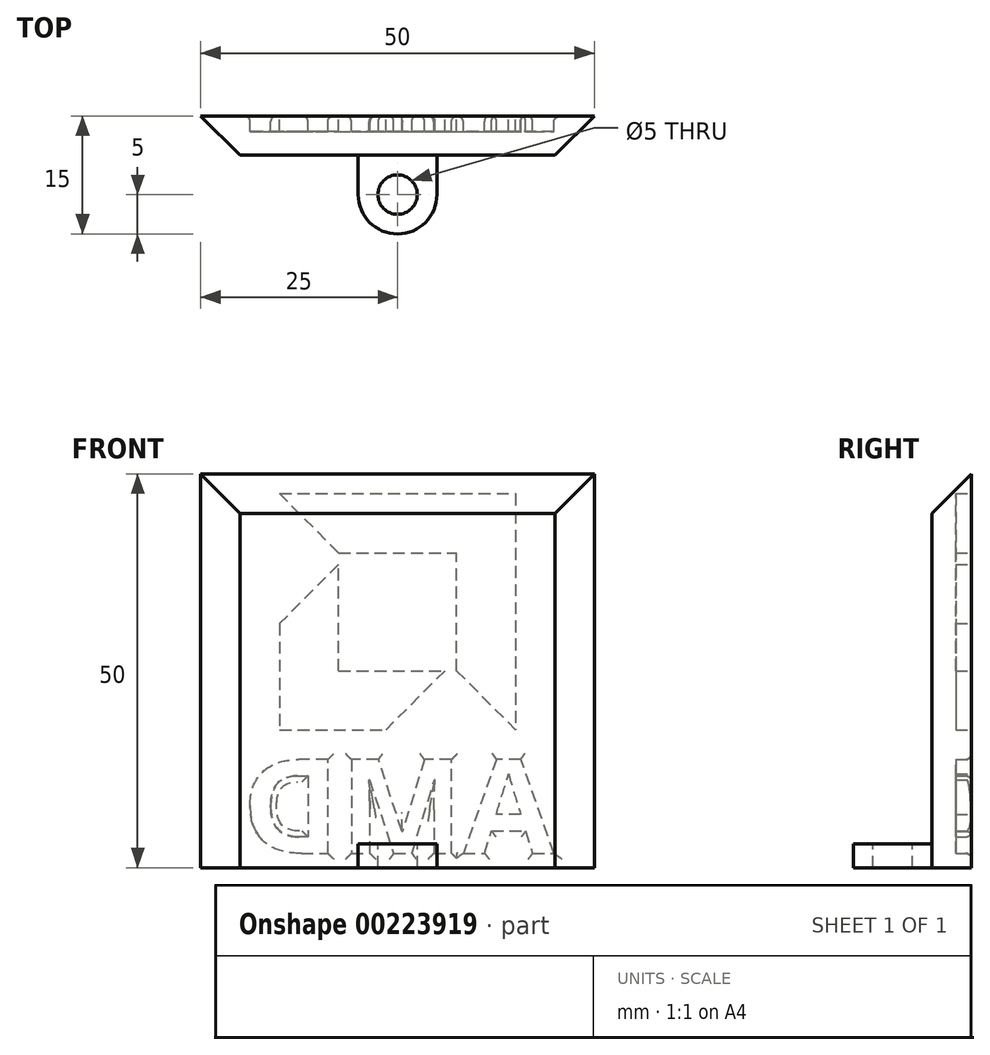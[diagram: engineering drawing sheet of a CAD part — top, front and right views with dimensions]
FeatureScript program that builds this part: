
annotation { "Feature Type Name" : "Feature", "Feature Type Description" : "" }
export const myFeature = defineFeature(function(context is Context, id is Id, definition is map)
    precondition{}
    {
        {
            var Q0;
            Q0=qCreatedBy(makeId("Front.planeOp"),FACE);
            var sketch = newSketch(context, id + "F0", { "sketchPlane" : qUnion([Q0])});
            skLineSegment(sketch, "E0.bottom", {"start": v(0, 0) * mm, "end": v(50, 0) * mm});
            skLineSegment(sketch, "E0.top", {"start": v(0, 50) * mm, "end": v(50, 50) * mm});
            skLineSegment(sketch, "E0.left", {"start": v(0, 0) * mm, "end": v(0, 50) * mm});
            skLineSegment(sketch, "E0.right", {"start": v(50, 0) * mm, "end": v(50, 50) * mm});
            skLineSegment(sketch, "E1.bottom", {"start": v(10, 47.5) * mm, "end": v(40, 47.5) * mm});
            skLineSegment(sketch, "E1.top", {"start": v(10, 17.5) * mm, "end": v(40, 17.5) * mm});
            skLineSegment(sketch, "E1.left", {"start": v(10, 47.5) * mm, "end": v(10, 17.5) * mm});
            skLineSegment(sketch, "E1.right", {"start": v(40, 47.5) * mm, "end": v(40, 17.5) * mm});
            skLineSegment(sketch, "E2.bottom", {"start": v(17.5, 25) * mm, "end": v(32.5, 25) * mm});
            skLineSegment(sketch, "E2.top", {"start": v(17.5, 40) * mm, "end": v(32.5, 40) * mm});
            skLineSegment(sketch, "E2.left", {"start": v(17.5, 25) * mm, "end": v(17.5, 40) * mm});
            skLineSegment(sketch, "E2.right", {"start": v(32.5, 25) * mm, "end": v(32.5, 40) * mm});
            skLineSegment(sketch, "E3", {"start": v(17.5, 40) * mm, "end": v(10, 47.5) * mm});
            skLineSegment(sketch, "E4", {"start": v(32.5, 25) * mm, "end": v(40, 17.5) * mm});
            skPoint(sketch, "E5", {"position": v(17.5, 38.5) * mm});
            skPoint(sketch, "E6", {"position": v(31, 25) * mm});
            skLineSegment(sketch, "E7", {"start": v(17.5, 38.5) * mm, "end": v(10, 31) * mm});
            skLineSegment(sketch, "E8", {"start": v(31, 25) * mm, "end": v(23.5, 17.5) * mm});
            skSolve(sketch);
        }
        {
            var Q0;
            Q0=makeQuery(id+"F0.imprint","IMPRINT",FACE,{"disambiguationData":[TD([[makeQuery(id+"F0.imprint","IMPRINT",EDGE,{"derivedFrom":sQuery(id+"F0.wireOp",EDGE,"E0.bottom")}),1.0]])]});
            var Q1;
            {var subQ0=sQuery(id+"F0.wireOp",EDGE,"E3");Q1=makeQuery(id+"F0.imprint","IMPRINT",FACE,{"disambiguationData":[TD([[makeQuery(id+"F0.imprint","IMPRINT",EDGE,{"derivedFrom":subQ0}),1.0]])]});}
            var Q2;
            Q2=makeQuery(id+"F0.imprint","IMPRINT",FACE,{"disambiguationData":[TD([[makeQuery(id+"F0.imprint","IMPRINT",EDGE,{"derivedFrom":sQuery(id+"F0.wireOp",EDGE,"E1.bottom")}),-1.0]])]});
            var Q3;
            {var subQ4=sQuery(id+"F0.wireOp",EDGE,"E2.top");Q3=makeQuery(id+"F0.imprint","IMPRINT",FACE,{"disambiguationData":[TD([[makeQuery(id+"F0.imprint","IMPRINT",EDGE,{"derivedFrom":subQ4}),-1.0]])]});}
            var Q4;
            {var subQ3=sQuery(id+"F0.wireOp",EDGE,"E7");Q4=makeQuery(id+"F0.imprint","IMPRINT",FACE,{"disambiguationData":[TD([[makeQuery(id+"F0.imprint","IMPRINT",EDGE,{"derivedFrom":subQ3}),1.0]])]});}
            var Q5;
            {var subQ0=sQuery(id+"F0.wireOp",EDGE,"E4");Q5=makeQuery(id+"F0.imprint","IMPRINT",FACE,{"disambiguationData":[TD([[makeQuery(id+"F0.imprint","IMPRINT",EDGE,{"derivedFrom":subQ0}),-1.0]])]});}
            extrude(context, id + "F1", {"entities" : qUnion([Q0, Q1, Q2, Q3, Q4, Q5]), "depth" : 5 * mm});
        }
        {
            var Q0;
            Q0=makeQuery(id+"F0.imprint","IMPRINT",FACE,{"disambiguationData":[TD([[makeQuery(id+"F0.imprint","IMPRINT",EDGE,{"derivedFrom":sQuery(id+"F0.wireOp",EDGE,"E1.bottom")}),-1.0]])]});
            var Q1;
            {var subQ3=sQuery(id+"F0.wireOp",EDGE,"E7");Q1=makeQuery(id+"F0.imprint","IMPRINT",FACE,{"disambiguationData":[TD([[makeQuery(id+"F0.imprint","IMPRINT",EDGE,{"derivedFrom":subQ3}),1.0]])]});}
            extrude(context, id + "F2", {"entities" : qUnion([Q0, Q1]), "operationType" : NewBodyOperationType.REMOVE, "depth" : 2 * mm});
        }
        {
            var Q0;
            Q0=makeQuery(id+"F1.opExtrude","CAP_FACE",FACE,{"disambiguationData":[OSD([sQuery(id+"F0.wireOp",EDGE,"E0.bottom"),sQuery(id+"F0.wireOp",EDGE,"E0.top"),sQuery(id+"F0.wireOp",EDGE,"E0.left"),sQuery(id+"F0.wireOp",EDGE,"E0.right")])],"isStart":true});
            var sketch = newSketch(context, id + "F3", { "sketchPlane" : qUnion([Q0])});
            skText(sketch, "E9", { "text": "AMD", "fontName": "OpenSans-Bold.ttf"});
            const initialGuessF3  = {"E9": [-0.04485, 0.00182, 1, 0, 0.012]};
            skSetInitialGuess(sketch, initialGuessF3);
            skSolve(sketch);
        }
        {
            var Q0;
            Q0 = qSketchRegion(id + "F3", true);
            extrude(context, id + "F4", {"entities" : qUnion([Q0]), "operationType" : NewBodyOperationType.REMOVE, "oppositeDirection" : true, "depth" : 2 * mm});
        }
        {
            var Q0;
            Q0=makeQuery(id+"F1.opExtrude","SWEPT_FACE",FACE,{"disambiguationData":[OSD([sQuery(id+"F0.wireOp",EDGE,"E0.top")])]});
            var sketch = newSketch(context, id + "F5", { "sketchPlane" : qUnion([Q0])});
            skLineSegment(sketch, "E10", {"start": v(0, 0) * mm, "end": v(4.65, -4.65) * mm});
            skLineSegment(sketch, "E11", {"start": v(0, 0) * mm, "end": v(5, -5) * mm});
            skLineSegment(sketch, "E12", {"start": v(5, -5) * mm, "end": v(0, -5) * mm});
            skLineSegment(sketch, "E13", {"start": v(0, -5) * mm, "end": v(0, 0) * mm});
            skLineSegment(sketch, "E14", {"start": v(50, 0) * mm, "end": v(50, -5) * mm});
            skLineSegment(sketch, "E15", {"start": v(50, -5) * mm, "end": v(45, -5) * mm});
            skLineSegment(sketch, "E16", {"start": v(45, -5) * mm, "end": v(50, 0) * mm});
            skSolve(sketch);
        }
        {
            var Q0;
            Q0=makeQuery(id+"F1.opExtrude","SWEPT_FACE",FACE,{"disambiguationData":[OSD([sQuery(id+"F0.wireOp",EDGE,"E0.left")])]});
            var sketch = newSketch(context, id + "F6", { "sketchPlane" : qUnion([Q0])});
            skLineSegment(sketch, "E17", {"start": v(5, 50) * mm, "end": v(5, 45) * mm});
            skLineSegment(sketch, "E18", {"start": v(5, 45) * mm, "end": v(0, 50) * mm});
            skSolve(sketch);
        }
        {
            var Q0;
            Q0 = qSketchRegion(id + "F6", true);
            var Q1;
            Q1=makeQuery(id+"F6.imprint","IMPRINT",FACE,{"disambiguationData":[TD([[makeQuery(id+"F6.imprint","IMPRINT",EDGE,{"derivedFrom":sQuery(id+"F6.wireOp",EDGE,"E17")}),1.0]])]});
            extrude(context, id + "F7", {"entities" : qUnion([Q0, Q1]), "operationType" : NewBodyOperationType.REMOVE, "oppositeDirection" : true, "depth" : 50 * mm});
        }
        {
            var Q0;
            Q0 = qSketchRegion(id + "F5", true);
            extrude(context, id + "F8", {"entities" : qUnion([Q0]), "operationType" : NewBodyOperationType.REMOVE, "oppositeDirection" : true, "depth" : 50 * mm});
        }
        {
            var Q0;
            Q0=makeQuery(id+"F1.opExtrude","CAP_FACE",FACE,{"disambiguationData":[OSD([sQuery(id+"F0.wireOp",EDGE,"E0.bottom"),sQuery(id+"F0.wireOp",EDGE,"E0.top"),sQuery(id+"F0.wireOp",EDGE,"E0.left"),sQuery(id+"F0.wireOp",EDGE,"E0.right")])],"isStart":false});
            var sketch = newSketch(context, id + "F9", { "sketchPlane" : qUnion([Q0])});
            skPoint(sketch, "E19", {"position": v(25, 0) * mm});
            skLineSegment(sketch, "E20", {"start": v(25, 0) * mm, "end": v(20, 0) * mm});
            skLineSegment(sketch, "E21", {"start": v(25, 0) * mm, "end": v(30, 0) * mm});
            skLineSegment(sketch, "E22", {"start": v(20, 0) * mm, "end": v(20, 3) * mm});
            skLineSegment(sketch, "E23", {"start": v(20, 3) * mm, "end": v(30, 3) * mm});
            skLineSegment(sketch, "E24", {"start": v(30, 3) * mm, "end": v(30, 0) * mm});
            skSolve(sketch);
        }
        {
            var Q0;
            Q0 = qSketchRegion(id + "F9", true);
            extrude(context, id + "F10", {"entities" : qUnion([Q0]), "operationType" : NewBodyOperationType.ADD, "depth" : 10 * mm});
        }
        {
            var Q0;
            Q0=makeQuery(id+"F10.opExtrude","SWEPT_FACE",FACE,{"disambiguationData":[OSD([sQuery(id+"F9.wireOp",EDGE,"E23")])]});
            var sketch = newSketch(context, id + "F11", { "sketchPlane" : qUnion([Q0])});
            skLineSegment(sketch, "E25", {"start": v(25, -5) * mm, "end": v(25, -15) * mm});
            skLineSegment(sketch, "E26", {"start": v(20, -10) * mm, "end": v(30, -10) * mm});
            skCircle(sketch, "E27", {"center": v(25, -10) * mm, "radius": 2.5 * mm});
            skSolve(sketch);
        }
        {
            var Q0;
            {var subQ0=sQuery(id+"F11.wireOp",EDGE,"E27");var subQ1=sQuery(id+"F11.wireOp",EDGE,"E25");var subQ2=makeQuery(id+"F11.imprint","INTERSECT",VERTEX,{"disambiguationData":[OD(0.0)],"derivedFrom":[subQ1,subQ0]});Q0=makeQuery(id+"F11.imprint","IMPRINT",FACE,{"disambiguationData":[TD([[makeQuery(id+"F11.imprint","IMPRINT",EDGE,{"disambiguationData":[TD([[subQ2,-1.0]])],"derivedFrom":subQ1}),-1.0]])]});}
            var Q1;
            {var subQ0=sQuery(id+"F11.wireOp",EDGE,"E27");var subQ1=sQuery(id+"F11.wireOp",EDGE,"E25");var subQ2=makeQuery(id+"F11.imprint","INTERSECT",VERTEX,{"disambiguationData":[OD(0.0)],"derivedFrom":[subQ1,subQ0]});Q1=makeQuery(id+"F11.imprint","IMPRINT",FACE,{"disambiguationData":[TD([[makeQuery(id+"F11.imprint","IMPRINT",EDGE,{"disambiguationData":[TD([[subQ2,-1.0]])],"derivedFrom":subQ1}),1.0]])]});}
            var Q2;
            {var subQ0=sQuery(id+"F11.wireOp",EDGE,"E26");var subQ1=sQuery(id+"F11.wireOp",EDGE,"E25");var subQ2=makeQuery(id+"F11.imprint","INTERSECT",VERTEX,{"derivedFrom":[subQ1,subQ0]});Q2=makeQuery(id+"F11.imprint","IMPRINT",FACE,{"disambiguationData":[TD([[makeQuery(id+"F11.imprint","IMPRINT",EDGE,{"disambiguationData":[TD([[subQ2,-1.0]])],"derivedFrom":subQ1}),1.0]])]});}
            var Q3;
            {var subQ0=sQuery(id+"F11.wireOp",EDGE,"E26");var subQ1=sQuery(id+"F11.wireOp",EDGE,"E25");var subQ2=makeQuery(id+"F11.imprint","INTERSECT",VERTEX,{"derivedFrom":[subQ1,subQ0]});Q3=makeQuery(id+"F11.imprint","IMPRINT",FACE,{"disambiguationData":[TD([[makeQuery(id+"F11.imprint","IMPRINT",EDGE,{"disambiguationData":[TD([[subQ2,-1.0]])],"derivedFrom":subQ1}),-1.0]])]});}
            extrude(context, id + "F12", {"entities" : qUnion([Q0, Q1, Q2, Q3]), "operationType" : NewBodyOperationType.REMOVE, "oppositeDirection" : true, "depth" : 25 * mm});
        }
        {
            var Q0;
            Q0=makeQuery(id+"F10.opExtrude","CAP_EDGE",EDGE,{"disambiguationData":[OSD([sQuery(id+"F9.wireOp",EDGE,"E22")])],"isStart":false});
            var Q1;
            Q1=makeQuery(id+"F10.opExtrude","CAP_EDGE",EDGE,{"disambiguationData":[OSD([sQuery(id+"F9.wireOp",EDGE,"E24")])],"isStart":false});
            fillet(context, id + "F13", {"entities" : qUnion([Q0, Q1]), "radius" : 5 * mm, "tangentPropagation" : true, "allowEdgeOverflow" : false});
        }
        {
            var Q0;
            Q0=makeQuery(id+"F4.boolean.opBoolean","COPY",EDGE,{"derivedFrom":makeQuery(id+"F4.opExtrude","CAP_EDGE",EDGE,{"disambiguationData":[OSD([sQuery(id+"F3.wireOp",EDGE,"E9.sketch_text.stroke-34")])],"isStart":true})});
            var Q1;
            Q1=makeQuery(id+"F4.boolean.opBoolean","COPY",EDGE,{"derivedFrom":makeQuery(id+"F4.opExtrude","CAP_EDGE",EDGE,{"disambiguationData":[OSD([sQuery(id+"F3.wireOp",EDGE,"E9.sketch_text.stroke-40")])],"isStart":true})});
            var Q2;
            Q2=makeQuery(id+"F4.boolean.opBoolean","COPY",EDGE,{"derivedFrom":makeQuery(id+"F4.opExtrude","CAP_EDGE",EDGE,{"disambiguationData":[OSD([sQuery(id+"F3.wireOp",EDGE,"E9.sketch_text.stroke-42")])],"isStart":true})});
            var Q3;
            Q3=makeQuery(id+"F4.boolean.opBoolean","COPY",EDGE,{"derivedFrom":makeQuery(id+"F4.opExtrude","CAP_EDGE",EDGE,{"disambiguationData":[OSD([sQuery(id+"F3.wireOp",EDGE,"E9.sketch_text.stroke-38")])],"isStart":true})});
            var Q4;
            Q4=makeQuery(id+"F4.boolean.opBoolean","COPY",EDGE,{"derivedFrom":makeQuery(id+"F4.opExtrude","CAP_EDGE",EDGE,{"disambiguationData":[OSD([sQuery(id+"F3.wireOp",EDGE,"E9.sketch_text.stroke-41")])],"isStart":true})});
            var Q5;
            Q5=makeQuery(id+"F4.boolean.opBoolean","COPY",EDGE,{"derivedFrom":makeQuery(id+"F4.opExtrude","CAP_EDGE",EDGE,{"disambiguationData":[OSD([sQuery(id+"F3.wireOp",EDGE,"E9.sketch_text.stroke-39")])],"isStart":true})});
            var Q6;
            Q6=makeQuery(id+"F4.boolean.opBoolean","COPY",EDGE,{"derivedFrom":makeQuery(id+"F4.opExtrude","CAP_EDGE",EDGE,{"disambiguationData":[OSD([sQuery(id+"F3.wireOp",EDGE,"E9.sketch_text.stroke-36")])],"isStart":true})});
            var Q7;
            Q7=makeQuery(id+"F4.boolean.opBoolean","COPY",EDGE,{"derivedFrom":makeQuery(id+"F4.opExtrude","CAP_EDGE",EDGE,{"disambiguationData":[OSD([sQuery(id+"F3.wireOp",EDGE,"E9.sketch_text.stroke-35")])],"isStart":true})});
            var Q8;
            Q8=makeQuery(id+"F4.boolean.opBoolean","COPY",EDGE,{"derivedFrom":makeQuery(id+"F4.opExtrude","CAP_EDGE",EDGE,{"disambiguationData":[OSD([sQuery(id+"F3.wireOp",EDGE,"E9.sketch_text.stroke-31")])],"isStart":true})});
            var Q9;
            Q9=makeQuery(id+"F4.boolean.opBoolean","COPY",EDGE,{"derivedFrom":makeQuery(id+"F4.opExtrude","CAP_EDGE",EDGE,{"disambiguationData":[OSD([sQuery(id+"F3.wireOp",EDGE,"E9.sketch_text.stroke-37")])],"isStart":true})});
            var Q10;
            Q10=makeQuery(id+"F4.boolean.opBoolean","COPY",EDGE,{"derivedFrom":makeQuery(id+"F4.opExtrude","CAP_EDGE",EDGE,{"disambiguationData":[OSD([sQuery(id+"F3.wireOp",EDGE,"E9.sketch_text.stroke-32")])],"isStart":true})});
            var Q11;
            Q11=makeQuery(id+"F4.boolean.opBoolean","COPY",EDGE,{"derivedFrom":makeQuery(id+"F4.opExtrude","CAP_EDGE",EDGE,{"disambiguationData":[OSD([sQuery(id+"F3.wireOp",EDGE,"E9.sketch_text.stroke-33")])],"isStart":true})});
            var Q12;
            Q12=makeQuery(id+"F4.boolean.opBoolean","COPY",EDGE,{"derivedFrom":makeQuery(id+"F4.opExtrude","CAP_EDGE",EDGE,{"disambiguationData":[OSD([sQuery(id+"F3.wireOp",EDGE,"E9.sketch_text.stroke-23")])],"isStart":true})});
            var Q13;
            Q13=makeQuery(id+"F4.boolean.opBoolean","COPY",EDGE,{"derivedFrom":makeQuery(id+"F4.opExtrude","CAP_EDGE",EDGE,{"disambiguationData":[OSD([sQuery(id+"F3.wireOp",EDGE,"E9.sketch_text.stroke-24")])],"isStart":true})});
            var Q14;
            Q14=makeQuery(id+"F4.boolean.opBoolean","COPY",EDGE,{"derivedFrom":makeQuery(id+"F4.opExtrude","CAP_EDGE",EDGE,{"disambiguationData":[OSD([sQuery(id+"F3.wireOp",EDGE,"E9.sketch_text.stroke-25")])],"isStart":true})});
            var Q15;
            Q15=makeQuery(id+"F4.boolean.opBoolean","COPY",EDGE,{"derivedFrom":makeQuery(id+"F4.opExtrude","CAP_EDGE",EDGE,{"disambiguationData":[OSD([sQuery(id+"F3.wireOp",EDGE,"E9.sketch_text.stroke-26")])],"isStart":true})});
            var Q16;
            Q16=makeQuery(id+"F4.boolean.opBoolean","COPY",EDGE,{"derivedFrom":makeQuery(id+"F4.opExtrude","CAP_EDGE",EDGE,{"disambiguationData":[OSD([sQuery(id+"F3.wireOp",EDGE,"E9.sketch_text.stroke-27")])],"isStart":true})});
            var Q17;
            Q17=makeQuery(id+"F4.boolean.opBoolean","COPY",EDGE,{"derivedFrom":makeQuery(id+"F4.opExtrude","CAP_EDGE",EDGE,{"disambiguationData":[OSD([sQuery(id+"F3.wireOp",EDGE,"E9.sketch_text.stroke-29")])],"isStart":true})});
            var Q18;
            Q18=makeQuery(id+"F4.boolean.opBoolean","COPY",EDGE,{"derivedFrom":makeQuery(id+"F4.opExtrude","CAP_EDGE",EDGE,{"disambiguationData":[OSD([sQuery(id+"F3.wireOp",EDGE,"E9.sketch_text.stroke-30")])],"isStart":true})});
            var Q19;
            Q19=makeQuery(id+"F4.boolean.opBoolean","COPY",EDGE,{"derivedFrom":makeQuery(id+"F4.opExtrude","CAP_EDGE",EDGE,{"disambiguationData":[OSD([sQuery(id+"F3.wireOp",EDGE,"E9.sketch_text.stroke-12")])],"isStart":true})});
            var Q20;
            Q20=makeQuery(id+"F4.boolean.opBoolean","COPY",EDGE,{"derivedFrom":makeQuery(id+"F4.opExtrude","CAP_EDGE",EDGE,{"disambiguationData":[OSD([sQuery(id+"F3.wireOp",EDGE,"E9.sketch_text.stroke-15")])],"isStart":true})});
            var Q21;
            Q21=makeQuery(id+"F4.boolean.opBoolean","COPY",EDGE,{"derivedFrom":makeQuery(id+"F4.opExtrude","CAP_EDGE",EDGE,{"disambiguationData":[OSD([sQuery(id+"F3.wireOp",EDGE,"E9.sketch_text.stroke-14")])],"isStart":true})});
            var Q22;
            Q22=makeQuery(id+"F4.boolean.opBoolean","COPY",EDGE,{"derivedFrom":makeQuery(id+"F4.opExtrude","CAP_EDGE",EDGE,{"disambiguationData":[OSD([sQuery(id+"F3.wireOp",EDGE,"E9.sketch_text.stroke-16")])],"isStart":true})});
            var Q23;
            Q23=makeQuery(id+"F4.boolean.opBoolean","COPY",EDGE,{"derivedFrom":makeQuery(id+"F4.opExtrude","CAP_EDGE",EDGE,{"disambiguationData":[OSD([sQuery(id+"F3.wireOp",EDGE,"E9.sketch_text.stroke-17")])],"isStart":true})});
            var Q24;
            Q24=makeQuery(id+"F4.boolean.opBoolean","COPY",EDGE,{"derivedFrom":makeQuery(id+"F4.opExtrude","CAP_EDGE",EDGE,{"disambiguationData":[OSD([sQuery(id+"F3.wireOp",EDGE,"E9.sketch_text.stroke-18")])],"isStart":true})});
            var Q25;
            Q25=makeQuery(id+"F4.boolean.opBoolean","COPY",EDGE,{"derivedFrom":makeQuery(id+"F4.opExtrude","CAP_EDGE",EDGE,{"disambiguationData":[OSD([sQuery(id+"F3.wireOp",EDGE,"E9.sketch_text.stroke-19")])],"isStart":true})});
            var Q26;
            Q26=makeQuery(id+"F4.boolean.opBoolean","COPY",EDGE,{"derivedFrom":makeQuery(id+"F4.opExtrude","CAP_EDGE",EDGE,{"disambiguationData":[OSD([sQuery(id+"F3.wireOp",EDGE,"E9.sketch_text.stroke-21")])],"isStart":true})});
            var Q27;
            Q27=makeQuery(id+"F4.boolean.opBoolean","COPY",EDGE,{"derivedFrom":makeQuery(id+"F4.opExtrude","CAP_EDGE",EDGE,{"disambiguationData":[OSD([sQuery(id+"F3.wireOp",EDGE,"E9.sketch_text.stroke-22")])],"isStart":true})});
            var Q28;
            Q28=makeQuery(id+"F4.boolean.opBoolean","COPY",EDGE,{"derivedFrom":makeQuery(id+"F4.opExtrude","CAP_EDGE",EDGE,{"disambiguationData":[OSD([sQuery(id+"F3.wireOp",EDGE,"E9.sketch_text.stroke-6")])],"isStart":true})});
            var Q29;
            Q29=makeQuery(id+"F4.boolean.opBoolean","COPY",EDGE,{"derivedFrom":makeQuery(id+"F4.opExtrude","CAP_EDGE",EDGE,{"disambiguationData":[OSD([sQuery(id+"F3.wireOp",EDGE,"E9.sketch_text.stroke-7")])],"isStart":true})});
            var Q30;
            Q30=makeQuery(id+"F4.boolean.opBoolean","COPY",EDGE,{"derivedFrom":makeQuery(id+"F4.opExtrude","CAP_EDGE",EDGE,{"disambiguationData":[OSD([sQuery(id+"F3.wireOp",EDGE,"E9.sketch_text.stroke-0")])],"isStart":true})});
            var Q31;
            Q31=makeQuery(id+"F4.boolean.opBoolean","COPY",EDGE,{"derivedFrom":makeQuery(id+"F4.opExtrude","CAP_EDGE",EDGE,{"disambiguationData":[OSD([sQuery(id+"F3.wireOp",EDGE,"E9.sketch_text.stroke-1")])],"isStart":true})});
            var Q32;
            Q32=makeQuery(id+"F4.boolean.opBoolean","COPY",EDGE,{"derivedFrom":makeQuery(id+"F4.opExtrude","CAP_EDGE",EDGE,{"disambiguationData":[OSD([sQuery(id+"F3.wireOp",EDGE,"E9.sketch_text.stroke-2")])],"isStart":true})});
            var Q33;
            Q33=makeQuery(id+"F4.boolean.opBoolean","COPY",EDGE,{"derivedFrom":makeQuery(id+"F4.opExtrude","CAP_EDGE",EDGE,{"disambiguationData":[OSD([sQuery(id+"F3.wireOp",EDGE,"E9.sketch_text.stroke-3")])],"isStart":true})});
            var Q34;
            Q34=makeQuery(id+"F4.boolean.opBoolean","COPY",EDGE,{"derivedFrom":makeQuery(id+"F4.opExtrude","CAP_EDGE",EDGE,{"disambiguationData":[OSD([sQuery(id+"F3.wireOp",EDGE,"E9.sketch_text.stroke-4")])],"isStart":true})});
            var Q35;
            Q35=makeQuery(id+"F4.boolean.opBoolean","COPY",EDGE,{"derivedFrom":makeQuery(id+"F4.opExtrude","CAP_EDGE",EDGE,{"disambiguationData":[OSD([sQuery(id+"F3.wireOp",EDGE,"E9.sketch_text.stroke-5")])],"isStart":true})});
            var Q36;
            Q36=makeQuery(id+"F4.boolean.opBoolean","COPY",EDGE,{"derivedFrom":makeQuery(id+"F4.opExtrude","CAP_EDGE",EDGE,{"disambiguationData":[OSD([sQuery(id+"F3.wireOp",EDGE,"E9.sketch_text.stroke-10")])],"isStart":true})});
            var Q37;
            Q37=makeQuery(id+"F4.boolean.opBoolean","COPY",EDGE,{"derivedFrom":makeQuery(id+"F4.opExtrude","CAP_EDGE",EDGE,{"disambiguationData":[OSD([sQuery(id+"F3.wireOp",EDGE,"E9.sketch_text.stroke-11")])],"isStart":true})});
            var Q38;
            Q38=makeQuery(id+"F4.boolean.opBoolean","COPY",EDGE,{"derivedFrom":makeQuery(id+"F4.opExtrude","CAP_EDGE",EDGE,{"disambiguationData":[OSD([sQuery(id+"F3.wireOp",EDGE,"E9.sketch_text.stroke-8")])],"isStart":true})});
            var Q39;
            Q39=makeQuery(id+"F4.boolean.opBoolean","COPY",EDGE,{"derivedFrom":makeQuery(id+"F4.opExtrude","CAP_EDGE",EDGE,{"disambiguationData":[OSD([sQuery(id+"F3.wireOp",EDGE,"E9.sketch_text.stroke-9")])],"isStart":true})});
            var Q40;
            Q40=makeQuery(id+"F2.boolean.opBoolean","COPY",EDGE,{"derivedFrom":makeQuery(id+"F2.opExtrude","CAP_EDGE",EDGE,{"disambiguationData":[OSD([sQuery(id+"F0.wireOp",EDGE,"E8")])],"isStart":true})});
            var Q41;
            Q41=makeQuery(id+"F2.boolean.opBoolean","COPY",EDGE,{"derivedFrom":makeQuery(id+"F2.opExtrude","CAP_EDGE",EDGE,{"disambiguationData":[OSD([sQuery(id+"F0.wireOp",EDGE,"E1.top")])],"isStart":true})});
            var Q42;
            Q42=makeQuery(id+"F2.boolean.opBoolean","COPY",EDGE,{"derivedFrom":makeQuery(id+"F2.opExtrude","CAP_EDGE",EDGE,{"disambiguationData":[OSD([sQuery(id+"F0.wireOp",EDGE,"E1.left")])],"isStart":true})});
            var Q43;
            Q43=makeQuery(id+"F2.boolean.opBoolean","COPY",EDGE,{"derivedFrom":makeQuery(id+"F2.opExtrude","CAP_EDGE",EDGE,{"disambiguationData":[OSD([sQuery(id+"F0.wireOp",EDGE,"E7")])],"isStart":true})});
            var Q44;
            Q44=makeQuery(id+"F2.boolean.opBoolean","COPY",EDGE,{"derivedFrom":makeQuery(id+"F2.opExtrude","CAP_EDGE",EDGE,{"disambiguationData":[OSD([sQuery(id+"F0.wireOp",EDGE,"E2.left")])],"isStart":true})});
            var Q45;
            Q45=makeQuery(id+"F2.boolean.opBoolean","COPY",EDGE,{"derivedFrom":makeQuery(id+"F2.opExtrude","CAP_EDGE",EDGE,{"disambiguationData":[OSD([sQuery(id+"F0.wireOp",EDGE,"E2.bottom")])],"isStart":true})});
            var Q46;
            Q46=makeQuery(id+"F2.boolean.opBoolean","COPY",EDGE,{"derivedFrom":makeQuery(id+"F2.opExtrude","CAP_EDGE",EDGE,{"disambiguationData":[OSD([sQuery(id+"F0.wireOp",EDGE,"E4")])],"isStart":true})});
            var Q47;
            Q47=makeQuery(id+"F2.boolean.opBoolean","COPY",EDGE,{"derivedFrom":makeQuery(id+"F2.opExtrude","CAP_EDGE",EDGE,{"disambiguationData":[OSD([sQuery(id+"F0.wireOp",EDGE,"E2.right")])],"isStart":true})});
            var Q48;
            Q48=makeQuery(id+"F2.boolean.opBoolean","COPY",EDGE,{"derivedFrom":makeQuery(id+"F2.opExtrude","CAP_EDGE",EDGE,{"disambiguationData":[OSD([sQuery(id+"F0.wireOp",EDGE,"E1.right")])],"isStart":true})});
            var Q49;
            Q49=makeQuery(id+"F2.boolean.opBoolean","COPY",EDGE,{"derivedFrom":makeQuery(id+"F2.opExtrude","CAP_EDGE",EDGE,{"disambiguationData":[OSD([sQuery(id+"F0.wireOp",EDGE,"E2.top")])],"isStart":true})});
            var Q50;
            Q50=makeQuery(id+"F2.boolean.opBoolean","COPY",EDGE,{"derivedFrom":makeQuery(id+"F2.opExtrude","CAP_EDGE",EDGE,{"disambiguationData":[OSD([sQuery(id+"F0.wireOp",EDGE,"E3")])],"isStart":true})});
            var Q51;
            Q51=makeQuery(id+"F2.boolean.opBoolean","COPY",EDGE,{"derivedFrom":makeQuery(id+"F2.opExtrude","CAP_EDGE",EDGE,{"disambiguationData":[OSD([sQuery(id+"F0.wireOp",EDGE,"E1.bottom")])],"isStart":true})});
            fillet(context, id + "F14", {"entities" : qUnion([Q0, Q1, Q2, Q3, Q4, Q5, Q6, Q7, Q8, Q9, Q10, Q11, Q12, Q13, Q14, Q15, Q16, Q17, Q18, Q19, Q20, Q21, Q22, Q23, Q24, Q25, Q26, Q27, Q28, Q29, Q30, Q31, Q32, Q33, Q34, Q35, Q36, Q37, Q38, Q39, Q40, Q41, Q42, Q43, Q44, Q45, Q46, Q47, Q48, Q49, Q50, Q51]), "radius" : .75 * mm, "tangentPropagation" : true, "allowEdgeOverflow" : false});
        }
        {
            var Q0;
            Q0=makeQuery(id+"F1.opExtrude","SWEPT_BODY",BODY,{"disambiguationData":[OSD([sQuery(id+"F0.wireOp",EDGE,"E0.bottom"),sQuery(id+"F0.wireOp",EDGE,"E0.top"),sQuery(id+"F0.wireOp",EDGE,"E0.left"),sQuery(id+"F0.wireOp",EDGE,"E0.right")])]});
            transform(context, id + "F15", {"entities" : qUnion([Q0]), "transformType" : TransformType.TRANSLATION_3D, "dx" : 0 * mm, "dy" : 0 * mm, "dz" : 0 * mm, "makeCopy" : true});
        }
        {
            var Q0;
            Q0=makeQuery(id+"F15.opPattern","COPY",BODY,{"derivedFrom":makeQuery(id+"F1.opExtrude","SWEPT_BODY",BODY,{"disambiguationData":[OSD([sQuery(id+"F0.wireOp",EDGE,"E0.bottom"),sQuery(id+"F0.wireOp",EDGE,"E0.top"),sQuery(id+"F0.wireOp",EDGE,"E0.left"),sQuery(id+"F0.wireOp",EDGE,"E0.right")])]}),"instanceName":"1"});
            deleteBodies(context, id + "F16", {"entities" : qUnion([Q0])});
        }
    });
